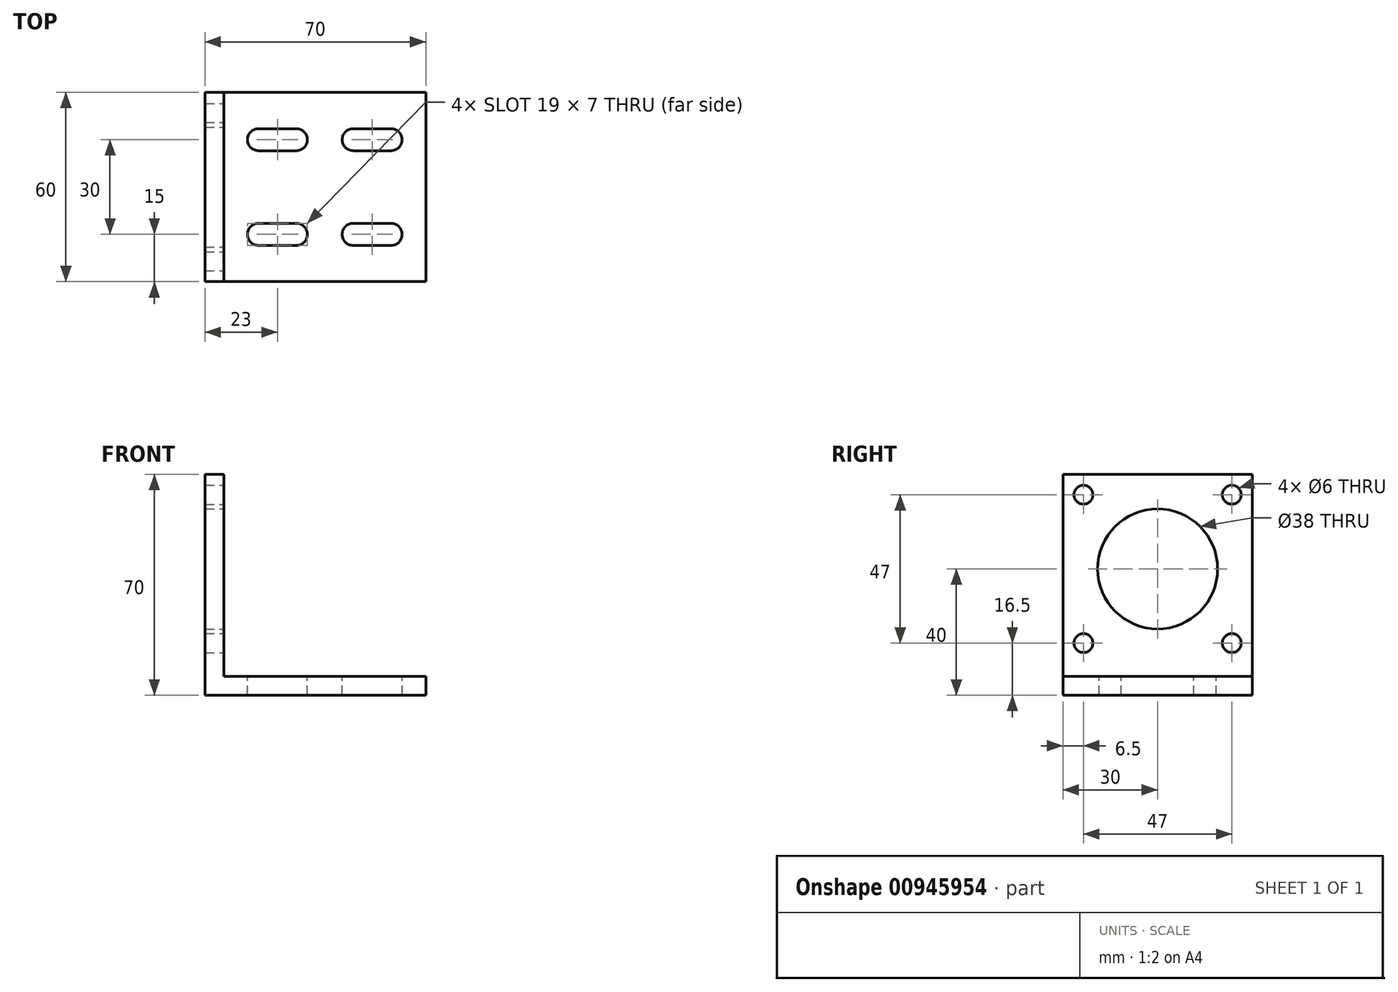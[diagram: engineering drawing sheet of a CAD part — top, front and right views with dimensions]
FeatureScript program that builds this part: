
annotation { "Feature Type Name" : "Feature", "Feature Type Description" : "" }
export const myFeature = defineFeature(function(context is Context, id is Id, definition is map)
    precondition{}
    {
        {
            var Q0;
            Q0=qCreatedBy(makeId("Front.planeOp"),FACE);
            var sketch = newSketch(context, id + "F0", { "sketchPlane" : qUnion([Q0])});
            skLineSegment(sketch, "E0.bottom", {"start": v(0, 0) * mm, "end": v(70, 0) * mm});
            skLineSegment(sketch, "E0.top", {"start": v(0, 70) * mm, "end": v(70, 70) * mm});
            skLineSegment(sketch, "E0.left", {"start": v(0, 0) * mm, "end": v(0, 70) * mm});
            skLineSegment(sketch, "E0.right", {"start": v(70, 0) * mm, "end": v(70, 70) * mm});
            skLineSegment(sketch, "E1.bottom", {"start": v(6, 6) * mm, "end": v(70, 6) * mm});
            skLineSegment(sketch, "E1.top", {"start": v(6, 70) * mm, "end": v(70, 70) * mm});
            skLineSegment(sketch, "E1.left", {"start": v(6, 6) * mm, "end": v(6, 70) * mm});
            skLineSegment(sketch, "E1.right", {"start": v(70, 6) * mm, "end": v(70, 70) * mm});
            skSolve(sketch);
        }
        {
            var Q0;
            Q0=makeQuery(id+"F0.imprint","IMPRINT",FACE,{"disambiguationData":[TD([[makeQuery(id+"F0.imprint","IMPRINT",EDGE,{"derivedFrom":sQuery(id+"F0.wireOp",EDGE,"E0.bottom")}),1.0]])]});
            extrude(context, id + "F1", {"entities" : qUnion([Q0]), "depth" : 30 * mm, "offsetDistance" : 25 * mm, "hasSecondDirection" : true, "secondDirectionOppositeDirection" : true, "secondDirectionDepth" : 30 * mm});
        }
        {
            var Q0;
            Q0=makeQuery(id+"F1.opExtrude","SWEPT_FACE",FACE,{"disambiguationData":[OSD([sQuery(id+"F0.wireOp",EDGE,"E1.left")])]});
            var sketch = newSketch(context, id + "F2", { "sketchPlane" : qUnion([Q0])});
            skLineSegment(sketch, "E2", {"start": v(0, 70) * mm, "end": v(0, 0) * mm, "construction": true});
            skCircle(sketch, "E3", {"center": v(0, 40) * mm, "radius": 19 * mm});
            skLineSegment(sketch, "E4.bottom", {"start": v(23.5, 63.5) * mm, "end": v(-23.5, 63.5) * mm, "construction": true});
            skLineSegment(sketch, "E4.top", {"start": v(23.5, 16.5) * mm, "end": v(-23.5, 16.5) * mm, "construction": true});
            skLineSegment(sketch, "E4.left", {"start": v(23.5, 63.5) * mm, "end": v(23.5, 16.5) * mm, "construction": true});
            skLineSegment(sketch, "E4.right", {"start": v(-23.5, 63.5) * mm, "end": v(-23.5, 16.5) * mm, "construction": true});
            skCircle(sketch, "E5", {"center": v(-23.5, 63.5) * mm, "radius": 3 * mm});
            skCircle(sketch, "E6", {"center": v(-23.5, 16.5) * mm, "radius": 3 * mm});
            skCircle(sketch, "E7.MirrorC", {"center": v(23.5, 16.5) * mm, "radius": 3 * mm});
            skCircle(sketch, "E8.MirrorC", {"center": v(23.5, 63.5) * mm, "radius": 3 * mm});
            skSolve(sketch);
        }
        {
            var Q0;
            Q0 = qSketchRegion(id + "F2", true);
            extrude(context, id + "F3", {"entities" : qUnion([Q0]), "operationType" : NewBodyOperationType.REMOVE, "endBound" : BoundingType.THROUGH_ALL, "oppositeDirection" : true, "depth" : 25 * mm, "offsetDistance" : 25 * mm});
        }
        {
            var Q0;
            Q0=makeQuery(id+"F1.opExtrude","SWEPT_FACE",FACE,{"disambiguationData":[OSD([sQuery(id+"F0.wireOp",EDGE,"E1.bottom")])]});
            var sketch = newSketch(context, id + "F4", { "sketchPlane" : qUnion([Q0])});
            skLineSegment(sketch, "E9.0.0", {"start": v(70, 30) * mm, "end": v(6, 30) * mm, "construction": true});
            skLineSegment(sketch, "E9.0.1", {"start": v(6, 30) * mm, "end": v(6, -30) * mm, "construction": true});
            skLineSegment(sketch, "E9.0.2", {"start": v(6, -30) * mm, "end": v(70, -30) * mm});
            skLineSegment(sketch, "E9.0.3", {"start": v(70, -30) * mm, "end": v(70, 30) * mm});
            skLineSegment(sketch, "E10.0.3", {"start": v(6, -30) * mm, "end": v(6, 30) * mm, "construction": true});
            skLineSegment(sketch, "E11.0.2", {"start": v(6, -30) * mm, "end": v(70, -30) * mm, "construction": true});
            skLineSegment(sketch, "E11.0.3", {"start": v(70, -30) * mm, "end": v(70, 30) * mm, "construction": true});
            skLineSegment(sketch, "E12", {"start": v(6, 0) * mm, "end": v(70, 0) * mm, "construction": true});
            skLineSegment(sketch, "E13.bottom", {"start": v(53, 15) * mm, "end": v(23, 15) * mm, "construction": true});
            skLineSegment(sketch, "E13.top", {"start": v(53, -15) * mm, "end": v(23, -15) * mm, "construction": true});
            skLineSegment(sketch, "E13.left", {"start": v(53, 15) * mm, "end": v(53, -15) * mm, "construction": true});
            skLineSegment(sketch, "E13.right", {"start": v(23, 15) * mm, "end": v(23, -15) * mm, "construction": true});
            skPoint(sketch, "E13.middle", {"position": v(38, 0) * mm});
            skLineSegment(sketch, "E14.bottom", {"start": v(29, -11.5) * mm, "end": v(17, -11.5) * mm});
            skLineSegment(sketch, "E14.top", {"start": v(29, -18.5) * mm, "end": v(17, -18.5) * mm});
            skLineSegment(sketch, "E14.left", {"start": v(29, -11.5) * mm, "end": v(29, -18.5) * mm, "construction": true});
            skLineSegment(sketch, "E14.right", {"start": v(17, -11.5) * mm, "end": v(17, -18.5) * mm, "construction": true});
            skPoint(sketch, "E14.middle", {"position": v(23, -15) * mm});
            skLineSegment(sketch, "E15.bottom", {"start": v(59, -11.5) * mm, "end": v(47, -11.5) * mm});
            skLineSegment(sketch, "E15.top", {"start": v(59, -18.5) * mm, "end": v(47, -18.5) * mm});
            skLineSegment(sketch, "E15.left", {"start": v(59, -11.5) * mm, "end": v(59, -18.5) * mm, "construction": true});
            skLineSegment(sketch, "E15.right", {"start": v(47, -11.5) * mm, "end": v(47, -18.5) * mm, "construction": true});
            skPoint(sketch, "E15.middle", {"position": v(53, -15) * mm});
            skArc(sketch, "E16", {"start": v(17, -11.5) * mm, "mid": v(13.5, -15) * mm, "end": v(17, -18.5) * mm});
            skArc(sketch, "E17", {"start": v(29, -18.5) * mm, "mid": v(32.5, -15) * mm, "end": v(29, -11.5) * mm});
            skLineSegment(sketch, "E18", {"start": v(38, 0) * mm, "end": v(38, 30) * mm, "construction": true});
            skArc(sketch, "E19.MirrorCS", {"start": v(47, -18.5) * mm, "mid": v(43.5, -15) * mm, "end": v(47, -11.5) * mm});
            skArc(sketch, "E20.MirrorCS", {"start": v(59, -11.5) * mm, "mid": v(62.5, -15) * mm, "end": v(59, -18.5) * mm});
            skArc(sketch, "E21.MirrorCS", {"start": v(59, 11.5) * mm, "mid": v(62.5, 15) * mm, "end": v(59, 18.5) * mm});
            skLineSegment(sketch, "E22.MirrorCS", {"start": v(59, 18.5) * mm, "end": v(47, 18.5) * mm});
            skLineSegment(sketch, "E23.MirrorCS", {"start": v(59, 11.5) * mm, "end": v(47, 11.5) * mm});
            skArc(sketch, "E24.MirrorCS", {"start": v(47, 18.5) * mm, "mid": v(43.5, 15) * mm, "end": v(47, 11.5) * mm});
            skArc(sketch, "E25.MirrorCS", {"start": v(29, 18.5) * mm, "mid": v(32.5, 15) * mm, "end": v(29, 11.5) * mm});
            skLineSegment(sketch, "E26.MirrorCS", {"start": v(29, 18.5) * mm, "end": v(17, 18.5) * mm});
            skLineSegment(sketch, "E27.MirrorCS", {"start": v(29, 11.5) * mm, "end": v(17, 11.5) * mm});
            skArc(sketch, "E28.MirrorCS", {"start": v(17, 11.5) * mm, "mid": v(13.5, 15) * mm, "end": v(17, 18.5) * mm});
            skSolve(sketch);
        }
        {
            var Q0;
            Q0 = qSketchRegion(id + "F4", true);
            extrude(context, id + "F5", {"entities" : qUnion([Q0]), "operationType" : NewBodyOperationType.REMOVE, "oppositeDirection" : true, "depth" : 25 * mm, "offsetDistance" : 25 * mm});
        }
    });
